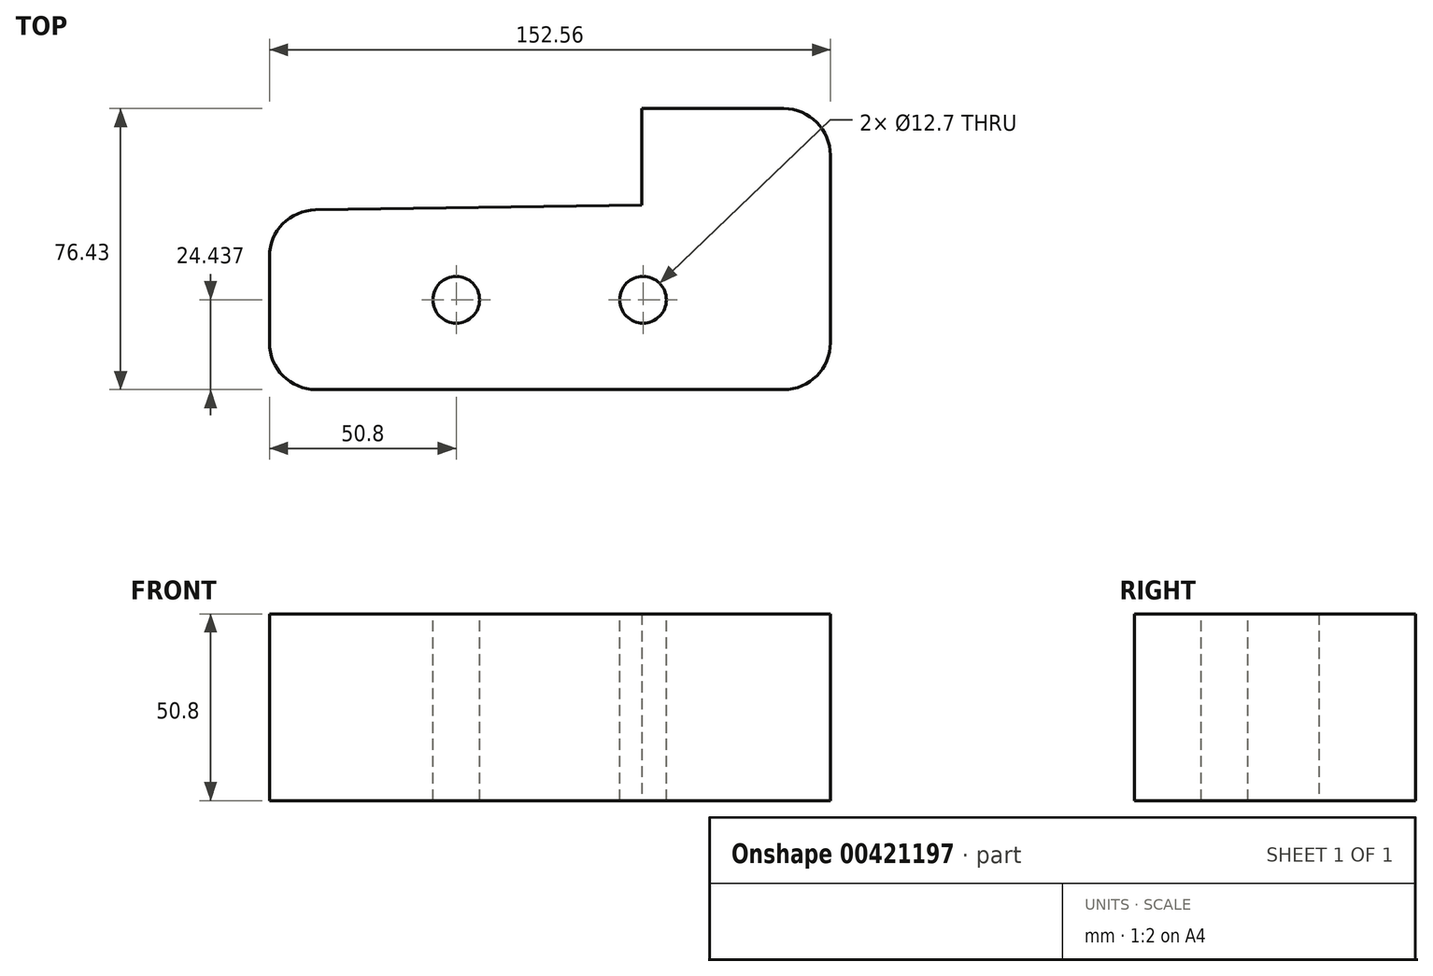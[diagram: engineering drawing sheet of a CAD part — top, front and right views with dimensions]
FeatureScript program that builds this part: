
annotation { "Feature Type Name" : "Feature", "Feature Type Description" : "" }
export const myFeature = defineFeature(function(context is Context, id is Id, definition is map)
    precondition{}
    {
        {
            var Q0;
            Q0=qCreatedBy(makeId("Top.planeOp"),FACE);
            var sketch = newSketch(context, id + "F0", { "sketchPlane" : qUnion([Q0])});
            skLineSegment(sketch, "E0", {"start": v(0, 0) * mm, "end": v(152.56, 0) * mm});
            skLineSegment(sketch, "E1", {"start": v(152.56, 0) * mm, "end": v(152.56, 76.43) * mm});
            skLineSegment(sketch, "E2", {"start": v(152.56, 76.43) * mm, "end": v(101.22, 76.43) * mm});
            skLineSegment(sketch, "E3", {"start": v(101.22, 76.43) * mm, "end": v(101.22, 50.17) * mm});
            skLineSegment(sketch, "E4", {"start": v(0, -2.36) * mm, "end": v(0, 48.7) * mm});
            skLineSegment(sketch, "E5", {"start": v(0, 48.7) * mm, "end": v(101.22, 50.17) * mm});
            skLineSegment(sketch, "E6", {"start": v(101.22, 50.17) * mm, "end": v(101.22, 48.7) * mm});
            skSolve(sketch);
        }
        {
            var Q0;
            {var subQ0=sQuery(id+"F0.wireOp",EDGE,"E0");Q0=makeQuery(id+"F0.imprint","IMPRINT",FACE,{"disambiguationData":[TD([[makeQuery(id+"F0.imprint","IMPRINT",EDGE,{"derivedFrom":subQ0}),1.0]])]});}
            extrude(context, id + "F1", {"entities" : qUnion([Q0]), "depth" : 50.8 * mm});
        }
        {
            var Q0;
            Q0=makeQuery(id+"F1.opExtrude","SWEPT_EDGE",EDGE,{"disambiguationData":[OSD([sQuery(id+"F0.wireOp",EDGE,"E0"),sQuery(id+"F0.wireOp",EDGE,"E1")])]});
            var Q1;
            Q1=makeQuery(id+"F1.opExtrude","SWEPT_EDGE",EDGE,{"disambiguationData":[OSD([sQuery(id+"F0.wireOp",EDGE,"E4"),sQuery(id+"F0.wireOp",EDGE,"E5")])]});
            var Q2;
            Q2=makeQuery(id+"F1.opExtrude","SWEPT_EDGE",EDGE,{"disambiguationData":[OSD([sQuery(id+"F0.wireOp",EDGE,"E0"),sQuery(id+"F0.wireOp",EDGE,"E4")])]});
            var Q3;
            Q3=makeQuery(id+"F1.opExtrude","SWEPT_EDGE",EDGE,{"disambiguationData":[OSD([sQuery(id+"F0.wireOp",EDGE,"E1"),sQuery(id+"F0.wireOp",EDGE,"E2")])]});
            fillet(context, id + "F2", {"entities" : qUnion([Q0, Q1, Q2, Q3]), "radius" : 12.7 * mm, "tangentPropagation" : true, "allowEdgeOverflow" : false});
        }
        {
            var Q0;
            Q0=makeQuery(id+"F1.opExtrude","CAP_FACE",FACE,{"disambiguationData":[OSD([sQuery(id+"F0.wireOp",EDGE,"E0"),sQuery(id+"F0.wireOp",EDGE,"E1"),sQuery(id+"F0.wireOp",EDGE,"E2"),sQuery(id+"F0.wireOp",EDGE,"E3"),sQuery(id+"F0.wireOp",EDGE,"E4"),sQuery(id+"F0.wireOp",EDGE,"E5")])],"isStart":false});
            var sketch = newSketch(context, id + "F3", { "sketchPlane" : qUnion([Q0])});
            skPoint(sketch, "E7", {"position": v(50.8, 24.44) * mm});
            skPoint(sketch, "E7.positionSnap0", {"position": v(0, 24.44) * mm});
            skPoint(sketch, "E8", {"position": v(101.6, 24.44) * mm});
            skSolve(sketch);
        }
        {
            var Q0;
            Q0=sQuery(id+"F3.wireOp",VERTEX,"E7");
            var Q1;
            Q1=sQuery(id+"F3.wireOp",VERTEX,"E8");
            var Q2;
            Q2=makeQuery(id+"F1.opExtrude","SWEPT_BODY",BODY,{"disambiguationData":[OSD([sQuery(id+"F0.wireOp",EDGE,"E0"),sQuery(id+"F0.wireOp",EDGE,"E1"),sQuery(id+"F0.wireOp",EDGE,"E2"),sQuery(id+"F0.wireOp",EDGE,"E3"),sQuery(id+"F0.wireOp",EDGE,"E4"),sQuery(id+"F0.wireOp",EDGE,"E5")])]});
            hole(context, id + "F4", {"style" : HoleStyle.SIMPLE, "endStyle" : HoleEndStyle.THROUGH, "holeDiameter" : 12.7 * mm, "isTappedThrough" : true, "tappedDepth" : 12.7 * mm, "tapClearance" : 3, "locations" : qUnion([Q0, Q1]), "scope" : qUnion([Q2])});
        }
    });
